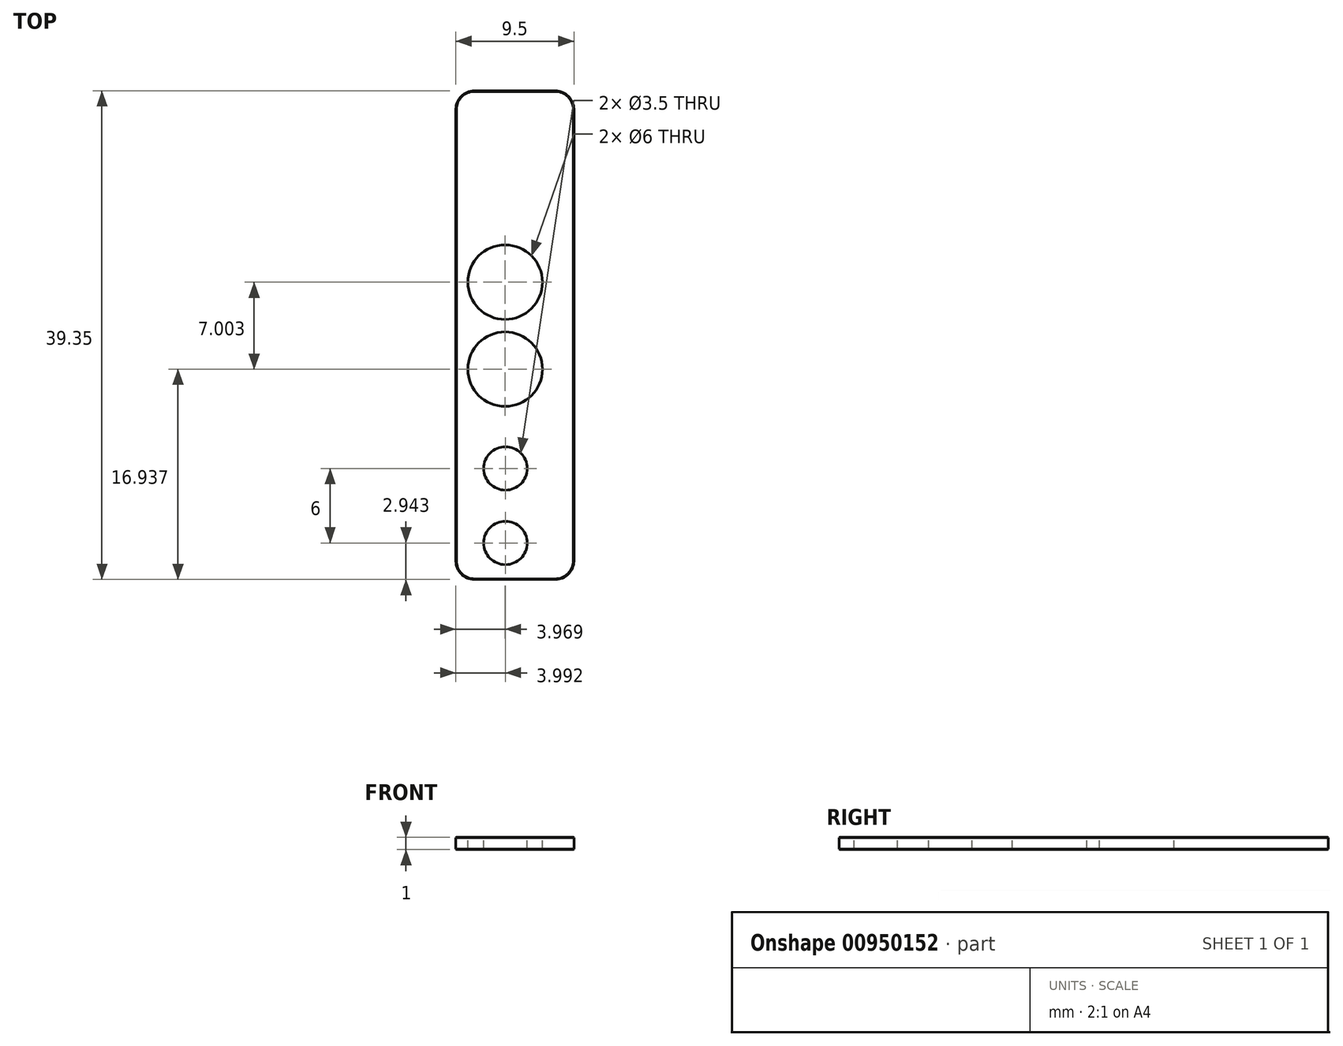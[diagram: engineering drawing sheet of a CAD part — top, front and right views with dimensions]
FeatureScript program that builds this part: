
annotation { "Feature Type Name" : "Feature", "Feature Type Description" : "" }
export const myFeature = defineFeature(function(context is Context, id is Id, definition is map)
    precondition{}
    {
        {
            var Q0;
            Q0=qCreatedBy(makeId("Top.planeOp"),FACE);
            var sketch = newSketch(context, id + "F0", { "sketchPlane" : qUnion([Q0])});
            skLineSegment(sketch, "E0", {"start": v(0, 1.5) * mm, "end": v(0, 37.85) * mm});
            skLineSegment(sketch, "E1", {"start": v(1.5, 39.35) * mm, "end": v(8, 39.35) * mm});
            skLineSegment(sketch, "E2", {"start": v(9.5, 37.85) * mm, "end": v(9.5, 1.5) * mm});
            skLineSegment(sketch, "E3", {"start": v(8, 0) * mm, "end": v(1.5, 0) * mm});
            skPoint(sketch, "E4.visualSharp", {"position": v(0, 39.35) * mm});
            skArc(sketch, "E4.filletArc", {"start": v(1.5, 39.35) * mm, "mid": v(0.44, 38.91) * mm, "end": v(0, 37.85) * mm});
            skPoint(sketch, "E5.visualSharp", {"position": v(9.5, 39.35) * mm});
            skArc(sketch, "E5.filletArc", {"start": v(9.5, 37.85) * mm, "mid": v(9.06, 38.91) * mm, "end": v(8, 39.35) * mm});
            skPoint(sketch, "E6.visualSharp", {"position": v(0, 0) * mm});
            skArc(sketch, "E6.filletArc", {"start": v(0, 1.5) * mm, "mid": v(0.44, 0.44) * mm, "end": v(1.5, 0) * mm});
            skPoint(sketch, "E7.visualSharp", {"position": v(9.5, 0) * mm});
            skArc(sketch, "E7.filletArc", {"start": v(8, 0) * mm, "mid": v(9.06, 0.44) * mm, "end": v(9.5, 1.5) * mm});
            skSolve(sketch);
        }
        {
            var Q0;
            Q0=makeQuery(id+"F0.imprint","IMPRINT",FACE,{"disambiguationData":[TD([[makeQuery(id+"F0.imprint","IMPRINT",EDGE,{"derivedFrom":sQuery(id+"F0.wireOp",EDGE,"E0")}),-1.0]])]});
            extrude(context, id + "F1", {"entities" : qUnion([Q0]), "oppositeDirection" : true, "depth" : 1 * mm, "offsetDistance" : 25 * mm});
        }
        {
            var Q0;
            Q0=qCreatedBy(makeId("Top.planeOp"),FACE);
            var sketch = newSketch(context, id + "F2", { "sketchPlane" : qUnion([Q0])});
            skCircle(sketch, "E8", {"center": v(4, 8.94) * mm, "radius": 1.75 * mm});
            skCircle(sketch, "E9", {"center": v(4, 2.94) * mm, "radius": 1.75 * mm});
            skSolve(sketch);
        }
        {
            var Q0;
            Q0=sQuery(id+"F2.wireOp",VERTEX,"E8.center");
            var Q1;
            Q1=sQuery(id+"F2.wireOp",VERTEX,"E9.center");
            var Q2;
            Q2=makeQuery(id+"F1.opExtrude","SWEPT_BODY",BODY,{"disambiguationData":[OSD([sQuery(id+"F0.wireOp",EDGE,"E0"),sQuery(id+"F0.wireOp",EDGE,"E1"),sQuery(id+"F0.wireOp",EDGE,"E2"),sQuery(id+"F0.wireOp",EDGE,"E3")])]});
            hole(context, id + "F3", {"style" : HoleStyle.SIMPLE, "endStyle" : HoleEndStyle.THROUGH, "holeDiameter" : 3.5 * mm, "majorDiameter" : 5 * mm, "tappedDepth" : 5.25 * mm, "tapClearance" : 3, "startFromSketch" : true, "locations" : qUnion([Q0, Q1]), "scope" : qUnion([Q2])});
        }
        {
            var Q0;
            Q0=makeQuery(id+"F1.opExtrude","CAP_FACE",FACE,{"disambiguationData":[OSD([sQuery(id+"F0.wireOp",EDGE,"E0"),sQuery(id+"F0.wireOp",EDGE,"E1"),sQuery(id+"F0.wireOp",EDGE,"E2"),sQuery(id+"F0.wireOp",EDGE,"E3")])],"isStart":true});
            var sketch = newSketch(context, id + "F4", { "sketchPlane" : qUnion([Q0])});
            skCircle(sketch, "E10", {"center": v(3.97, 23.94) * mm, "radius": 3 * mm});
            skCircle(sketch, "E11", {"center": v(3.97, 16.94) * mm, "radius": 3 * mm});
            skSolve(sketch);
        }
        {
            var Q0;
            Q0=sQuery(id+"F4.wireOp",VERTEX,"E10.center");
            var Q1;
            Q1=sQuery(id+"F4.wireOp",VERTEX,"E11.center");
            var Q2;
            Q2=makeQuery(id+"F1.opExtrude","SWEPT_BODY",BODY,{"disambiguationData":[OSD([sQuery(id+"F0.wireOp",EDGE,"E0"),sQuery(id+"F0.wireOp",EDGE,"E1"),sQuery(id+"F0.wireOp",EDGE,"E2"),sQuery(id+"F0.wireOp",EDGE,"E3")])]});
            hole(context, id + "F5", {"style" : HoleStyle.SIMPLE, "endStyle" : HoleEndStyle.THROUGH, "holeDiameter" : 6 * mm, "majorDiameter" : 5 * mm, "tappedDepth" : 5.25 * mm, "tapClearance" : 3, "startFromSketch" : true, "locations" : qUnion([Q0, Q1]), "scope" : qUnion([Q2])});
        }
        {
            var Q0;
            Q0=makeQuery(id+"F1.opExtrude","CAP_EDGE",EDGE,{"disambiguationData":[OSD([sQuery(id+"F0.wireOp",EDGE,"E2")])],"isStart":true});
            var Q1;
            Q1=makeQuery(id+"F1.opExtrude","CAP_EDGE",EDGE,{"disambiguationData":[OSD([sQuery(id+"F0.wireOp",EDGE,"E0")])],"isStart":true});
            var Q2;
            Q2=makeQuery(id+"F1.opExtrude","CAP_EDGE",EDGE,{"disambiguationData":[OSD([sQuery(id+"F0.wireOp",EDGE,"E3")])],"isStart":false});
            var Q3;
            Q3=makeQuery(id+"F1.opExtrude","SWEPT_EDGE",EDGE,{"disambiguationData":[OSD([sQuery(id+"F0.wireOp",EDGE,"E2"),sQuery(id+"F0.wireOp",EDGE,"E3")])]});
            var Q4;
            Q4=makeQuery(id+"F1.opExtrude","CAP_EDGE",EDGE,{"disambiguationData":[OSD([sQuery(id+"F0.wireOp",EDGE,"E3")])],"isStart":true});
            var Q5;
            Q5=makeQuery(id+"F1.opExtrude","SWEPT_EDGE",EDGE,{"disambiguationData":[OSD([sQuery(id+"F0.wireOp",EDGE,"E0"),sQuery(id+"F0.wireOp",EDGE,"E3")])]});
            var Q6;
            Q6=makeQuery(id+"F1.opExtrude","CAP_EDGE",EDGE,{"disambiguationData":[OSD([sQuery(id+"F0.wireOp",EDGE,"E2")])],"isStart":false});
            var Q7;
            Q7=makeQuery(id+"F1.opExtrude","SWEPT_EDGE",EDGE,{"disambiguationData":[OSD([sQuery(id+"F0.wireOp",EDGE,"E1"),sQuery(id+"F0.wireOp",EDGE,"E2")])]});
            var Q8;
            Q8=makeQuery(id+"F1.opExtrude","CAP_EDGE",EDGE,{"disambiguationData":[OSD([sQuery(id+"F0.wireOp",EDGE,"E1")])],"isStart":true});
            var Q9;
            Q9=makeQuery(id+"F1.opExtrude","CAP_EDGE",EDGE,{"disambiguationData":[OSD([sQuery(id+"F0.wireOp",EDGE,"E0")])],"isStart":false});
            var Q10;
            Q10=makeQuery(id+"F1.opExtrude","CAP_EDGE",EDGE,{"disambiguationData":[OSD([sQuery(id+"F0.wireOp",EDGE,"E1")])],"isStart":false});
            var Q11;
            Q11=makeQuery(id+"F1.opExtrude","SWEPT_EDGE",EDGE,{"disambiguationData":[OSD([sQuery(id+"F0.wireOp",EDGE,"E0"),sQuery(id+"F0.wireOp",EDGE,"E1")])]});
            chamfer(context, id + "F6", {"entities" : qUnion([Q0, Q1, Q2, Q3, Q4, Q5, Q6, Q7, Q8, Q9, Q10, Q11]), "width" : 0.05 * mm, "tangentPropagation" : true});
        }
    });
